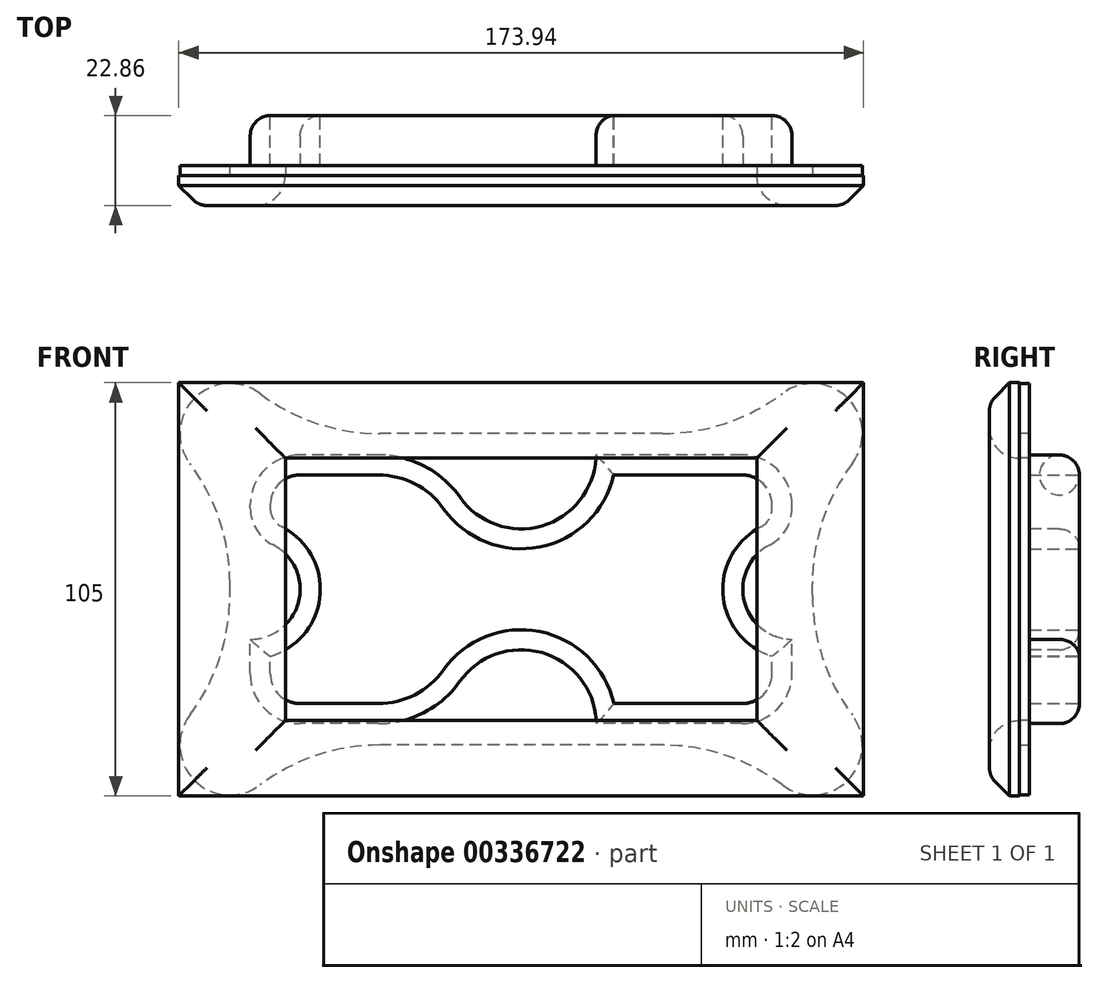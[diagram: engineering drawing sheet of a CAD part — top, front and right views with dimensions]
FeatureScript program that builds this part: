
annotation { "Feature Type Name" : "Feature", "Feature Type Description" : "" }
export const myFeature = defineFeature(function(context is Context, id is Id, definition is map)
    precondition{}
    {
        {
            var Q0;
            Q0=qCreatedBy(makeId("Front.planeOp"),FACE);
            var sketch = newSketch(context, id + "F0", { "sketchPlane" : qUnion([Q0])});
            skLineSegment(sketch, "E0.bottom", {"start": v(68.82, -34.13) * mm, "end": v(-68.82, -34.13) * mm});
            skLineSegment(sketch, "E0.top", {"start": v(68.82, 34.13) * mm, "end": v(-68.82, 34.13) * mm});
            skLineSegment(sketch, "E0.left", {"start": v(68.82, -34.13) * mm, "end": v(68.82, 34.13) * mm});
            skLineSegment(sketch, "E0.right", {"start": v(-68.82, -34.13) * mm, "end": v(-68.82, 34.13) * mm});
            skPoint(sketch, "E0.middle", {"position": v(0, 0) * mm});
            skSolve(sketch);
        }
        {
            var Q0;
            Q0 = qSketchRegion(id + "F0", true);
            extrude(context, id + "F1", {"entities" : qUnion([Q0]), "depth" : 12.7 * mm});
        }
        {
            var Q0;
            Q0=makeQuery(id+"F1.opExtrude","SWEPT_EDGE",EDGE,{"disambiguationData":[OSD([sQuery(id+"F0.wireOp",EDGE,"E0.top"),sQuery(id+"F0.wireOp",EDGE,"E0.right")])]});
            var Q1;
            Q1=makeQuery(id+"F1.opExtrude","SWEPT_EDGE",EDGE,{"disambiguationData":[OSD([sQuery(id+"F0.wireOp",EDGE,"E0.top"),sQuery(id+"F0.wireOp",EDGE,"E0.left")])]});
            var Q2;
            Q2=makeQuery(id+"F1.opExtrude","SWEPT_EDGE",EDGE,{"disambiguationData":[OSD([sQuery(id+"F0.wireOp",EDGE,"E0.bottom"),sQuery(id+"F0.wireOp",EDGE,"E0.left")])]});
            var Q3;
            Q3=makeQuery(id+"F1.opExtrude","SWEPT_EDGE",EDGE,{"disambiguationData":[OSD([sQuery(id+"F0.wireOp",EDGE,"E0.bottom"),sQuery(id+"F0.wireOp",EDGE,"E0.right")])]});
            fillet(context, id + "F2", {"entities" : qUnion([Q0, Q1, Q2, Q3]), "radius" : 12.7 * mm, "tangentPropagation" : true, "allowEdgeOverflow" : false});
        }
        {
            var Q0;
            Q0=makeQuery(id+"F1.opExtrude","CAP_FACE",FACE,{"disambiguationData":[OSD([sQuery(id+"F0.wireOp",EDGE,"E0.bottom"),sQuery(id+"F0.wireOp",EDGE,"E0.top"),sQuery(id+"F0.wireOp",EDGE,"E0.left"),sQuery(id+"F0.wireOp",EDGE,"E0.right")])],"isStart":false});
            var sketch = newSketch(context, id + "F3", { "sketchPlane" : qUnion([Q0])});
            skPoint(sketch, "E1", {"position": v(68.82, 0) * mm});
            skPoint(sketch, "E2", {"position": v(-68.82, 0) * mm});
            skPoint(sketch, "E3", {"position": v(0, 34.13) * mm});
            skPoint(sketch, "E4", {"position": v(0, -34.13) * mm});
            skCircle(sketch, "E5", {"center": v(-68.82, 0) * mm, "radius": 12.7 * mm});
            skSolve(sketch);
        }
        {
            var Q0;
            {var subQ3=sQuery(id+"F0.wireOp",EDGE,"E0.bottom");Q0=makeQuery(id+"F3.imprint","IMPRINT",FACE,{"disambiguationData":[TD([[makeQuery(id+"F3.imprint","IMPRINT",EDGE,{"derivedFrom":makeQuery(id+"F1.opExtrude","CAP_EDGE",EDGE,{"disambiguationData":[OSD([subQ3])],"isStart":false})}),-1.0]])]});}
            var sketch = newSketch(context, id + "F4", { "sketchPlane" : qUnion([Q0])});
            skCircle(sketch, "E6", {"center": v(69, 0) * mm, "radius": 12.7 * mm});
            skCircle(sketch, "E7", {"center": v(0, 34.4) * mm, "radius": 19.03 * mm});
            skCircle(sketch, "E8", {"center": v(0, -34.48) * mm, "radius": 19.12 * mm});
            skSolve(sketch);
        }
        {
            var Q0;
            {var subQ0=sQuery(id+"F4.wireOp",EDGE,"E8");var subQ1=makeQuery(id+"F3.imprint","IMPRINT",EDGE,{"derivedFrom":makeQuery(id+"F1.opExtrude","CAP_EDGE",EDGE,{"disambiguationData":[OSD([sQuery(id+"F0.wireOp",EDGE,"E0.bottom")])],"isStart":false})});var subQ2=makeQuery(id+"F4.imprint","INTERSECT",VERTEX,{"disambiguationData":[OD(0.0)],"derivedFrom":[subQ1,subQ0]});Q0=makeQuery(id+"F4.imprint","IMPRINT",FACE,{"disambiguationData":[TD([[makeQuery(id+"F4.imprint","IMPRINT",EDGE,{"disambiguationData":[TD([[subQ2,-1.0]])],"derivedFrom":subQ0}),1.0]])]});}
            var Q1;
            {var subQ0=sQuery(id+"F4.wireOp",EDGE,"E7");var subQ1=makeQuery(id+"F3.imprint","IMPRINT",EDGE,{"derivedFrom":makeQuery(id+"F1.opExtrude","CAP_EDGE",EDGE,{"disambiguationData":[OSD([sQuery(id+"F0.wireOp",EDGE,"E0.top")])],"isStart":false})});var subQ2=makeQuery(id+"F4.imprint","INTERSECT",VERTEX,{"disambiguationData":[OD(0.0)],"derivedFrom":[subQ1,subQ0]});Q1=makeQuery(id+"F4.imprint","IMPRINT",FACE,{"disambiguationData":[TD([[makeQuery(id+"F4.imprint","IMPRINT",EDGE,{"disambiguationData":[TD([[subQ2,1.0]])],"derivedFrom":subQ0}),1.0]])]});}
            extrude(context, id + "F5", {"entities" : qUnion([Q0, Q1]), "operationType" : NewBodyOperationType.REMOVE, "oppositeDirection" : true, "depth" : 25.4 * mm});
        }
        {
            var Q0;
            {var subQ0=sQuery(id+"F4.wireOp",EDGE,"E8");var subQ1=sQuery(id+"F0.wireOp",EDGE,"E0.bottom");Q0=makeQuery(id+"F5.boolean.opBoolean","COPY",EDGE,{"derivedFrom":makeQuery(id+"F5.opExtrude","SWEPT_EDGE",EDGE,{"disambiguationData":[OSD([subQ1,subQ0]),TDD([makeQuery(id+"F4.imprint","INTERSECT",VERTEX,{"disambiguationData":[OD(1.0)],"derivedFrom":[makeQuery(id+"F3.imprint","IMPRINT",EDGE,{"derivedFrom":makeQuery(id+"F1.opExtrude","CAP_EDGE",EDGE,{"disambiguationData":[OSD([subQ1])],"isStart":false})}),subQ0]})])]})});}
            var Q1;
            {var subQ0=sQuery(id+"F4.wireOp",EDGE,"E8");var subQ1=sQuery(id+"F0.wireOp",EDGE,"E0.bottom");Q1=makeQuery(id+"F5.boolean.opBoolean","COPY",EDGE,{"derivedFrom":makeQuery(id+"F5.opExtrude","SWEPT_EDGE",EDGE,{"disambiguationData":[OSD([subQ1,subQ0]),TDD([makeQuery(id+"F4.imprint","INTERSECT",VERTEX,{"disambiguationData":[OD(0.0)],"derivedFrom":[makeQuery(id+"F3.imprint","IMPRINT",EDGE,{"derivedFrom":makeQuery(id+"F1.opExtrude","CAP_EDGE",EDGE,{"disambiguationData":[OSD([subQ1])],"isStart":false})}),subQ0]})])]})});}
            var Q2;
            {var subQ0=sQuery(id+"F4.wireOp",EDGE,"E7");var subQ1=sQuery(id+"F0.wireOp",EDGE,"E0.top");Q2=makeQuery(id+"F5.boolean.opBoolean","COPY",EDGE,{"derivedFrom":makeQuery(id+"F5.opExtrude","SWEPT_EDGE",EDGE,{"disambiguationData":[OSD([subQ1,subQ0]),TDD([makeQuery(id+"F4.imprint","INTERSECT",VERTEX,{"disambiguationData":[OD(1.0)],"derivedFrom":[makeQuery(id+"F3.imprint","IMPRINT",EDGE,{"derivedFrom":makeQuery(id+"F1.opExtrude","CAP_EDGE",EDGE,{"disambiguationData":[OSD([subQ1])],"isStart":false})}),subQ0]})])]})});}
            var Q3;
            {var subQ0=sQuery(id+"F4.wireOp",EDGE,"E7");var subQ1=sQuery(id+"F0.wireOp",EDGE,"E0.top");Q3=makeQuery(id+"F5.boolean.opBoolean","COPY",EDGE,{"derivedFrom":makeQuery(id+"F5.opExtrude","SWEPT_EDGE",EDGE,{"disambiguationData":[OSD([subQ1,subQ0]),TDD([makeQuery(id+"F4.imprint","INTERSECT",VERTEX,{"disambiguationData":[OD(0.0)],"derivedFrom":[makeQuery(id+"F3.imprint","IMPRINT",EDGE,{"derivedFrom":makeQuery(id+"F1.opExtrude","CAP_EDGE",EDGE,{"disambiguationData":[OSD([subQ1])],"isStart":false})}),subQ0]})])]})});}
            fillet(context, id + "F6", {"entities" : qUnion([Q0, Q1, Q2, Q3]), "radius" : 25.4 * mm, "tangentPropagation" : true, "allowEdgeOverflow" : false});
        }
        {
            var Q0;
            {var subQ3=sQuery(id+"F0.wireOp",EDGE,"E0.bottom");Q0=makeQuery(id+"F3.imprint","IMPRINT",FACE,{"disambiguationData":[TD([[makeQuery(id+"F3.imprint","IMPRINT",EDGE,{"derivedFrom":makeQuery(id+"F1.opExtrude","CAP_EDGE",EDGE,{"disambiguationData":[OSD([subQ3])],"isStart":false})}),-1.0]])]});}
            var sketch = newSketch(context, id + "F7", { "sketchPlane" : qUnion([Q0])});
            skSolve(sketch);
        }
        {
            var Q0;
            {var subQ0=sQuery(id+"F3.wireOp",EDGE,"E5");var subQ1=makeQuery(id+"F1.opExtrude","CAP_EDGE",EDGE,{"disambiguationData":[OSD([sQuery(id+"F0.wireOp",EDGE,"E0.right")])],"isStart":false});var subQ2=makeQuery(id+"F3.imprint","INTERSECT",VERTEX,{"disambiguationData":[OD(0.0)],"derivedFrom":[subQ1,subQ0]});Q0=makeQuery(id+"F3.imprint","IMPRINT",FACE,{"disambiguationData":[TD([[makeQuery(id+"F3.imprint","IMPRINT",EDGE,{"disambiguationData":[TD([[subQ2,-1.0]])],"derivedFrom":subQ0}),1.0]])]});}
            var Q1;
            Q1=sQuery(id+"F3.wireOp",EDGE,"E5");
            extrude(context, id + "F8", {"entities" : qUnion([Q0]), "operationType" : NewBodyOperationType.REMOVE, "surfaceEntities" : qUnion([Q1]), "oppositeDirection" : true, "depth" : 25.4 * mm});
        }
        {
            var Q0;
            {var subQ3=sQuery(id+"F0.wireOp",EDGE,"E0.bottom");Q0=makeQuery(id+"F7.imprint","IMPRINT",FACE,{"disambiguationData":[TD([[makeQuery(id+"F7.imprint","IMPRINT",EDGE,{"derivedFrom":makeQuery(id+"F3.imprint","IMPRINT",EDGE,{"derivedFrom":makeQuery(id+"F1.opExtrude","CAP_EDGE",EDGE,{"disambiguationData":[OSD([subQ3])],"isStart":false})})}),-1.0]])]});}
            var sketch = newSketch(context, id + "F9", { "sketchPlane" : qUnion([Q0])});
            skPoint(sketch, "E9", {"position": v(69, 0) * mm});
            skCircle(sketch, "E10", {"center": v(69, 0) * mm, "radius": 12.7 * mm});
            skSolve(sketch);
        }
        {
            var Q0;
            {var subQ0=sQuery(id+"F9.wireOp",EDGE,"E10");var subQ1=makeQuery(id+"F7.imprint","IMPRINT",EDGE,{"derivedFrom":makeQuery(id+"F3.imprint","IMPRINT",EDGE,{"derivedFrom":makeQuery(id+"F1.opExtrude","CAP_EDGE",EDGE,{"disambiguationData":[OSD([sQuery(id+"F0.wireOp",EDGE,"E0.left")])],"isStart":false})})});var subQ2=makeQuery(id+"F9.imprint","INTERSECT",VERTEX,{"disambiguationData":[OD(0.0)],"derivedFrom":[subQ1,subQ0]});Q0=makeQuery(id+"F9.imprint","IMPRINT",FACE,{"disambiguationData":[TD([[makeQuery(id+"F9.imprint","IMPRINT",EDGE,{"disambiguationData":[TD([[subQ2,1.0]])],"derivedFrom":subQ0}),1.0]])]});}
            extrude(context, id + "F10", {"entities" : qUnion([Q0]), "operationType" : NewBodyOperationType.REMOVE, "oppositeDirection" : true, "depth" : 25.4 * mm});
        }
        {
            var Q0;
            {var subQ0=sQuery(id+"F3.wireOp",EDGE,"E5");var subQ1=sQuery(id+"F0.wireOp",EDGE,"E0.right");Q0=makeQuery(id+"F8.boolean.opBoolean","COPY",EDGE,{"derivedFrom":makeQuery(id+"F8.opExtrude","SWEPT_EDGE",EDGE,{"disambiguationData":[OSD([subQ1,subQ0]),TDD([makeQuery(id+"F3.imprint","INTERSECT",VERTEX,{"disambiguationData":[OD(1.0)],"derivedFrom":[makeQuery(id+"F1.opExtrude","CAP_EDGE",EDGE,{"disambiguationData":[OSD([subQ1])],"isStart":false}),subQ0]})])]})});}
            var Q1;
            {var subQ0=sQuery(id+"F3.wireOp",EDGE,"E5");var subQ1=sQuery(id+"F0.wireOp",EDGE,"E0.right");Q1=makeQuery(id+"F8.boolean.opBoolean","COPY",EDGE,{"derivedFrom":makeQuery(id+"F8.opExtrude","SWEPT_EDGE",EDGE,{"disambiguationData":[OSD([subQ1,subQ0]),TDD([makeQuery(id+"F3.imprint","INTERSECT",VERTEX,{"disambiguationData":[OD(0.0)],"derivedFrom":[makeQuery(id+"F1.opExtrude","CAP_EDGE",EDGE,{"disambiguationData":[OSD([subQ1])],"isStart":false}),subQ0]})])]})});}
            var Q2;
            {var subQ0=sQuery(id+"F9.wireOp",EDGE,"E10");var subQ1=sQuery(id+"F0.wireOp",EDGE,"E0.left");Q2=makeQuery(id+"F10.boolean.opBoolean","COPY",EDGE,{"derivedFrom":makeQuery(id+"F10.opExtrude","SWEPT_EDGE",EDGE,{"disambiguationData":[OSD([subQ1,subQ0]),TDD([makeQuery(id+"F9.imprint","INTERSECT",VERTEX,{"disambiguationData":[OD(0.0)],"derivedFrom":[makeQuery(id+"F7.imprint","IMPRINT",EDGE,{"derivedFrom":makeQuery(id+"F3.imprint","IMPRINT",EDGE,{"derivedFrom":makeQuery(id+"F1.opExtrude","CAP_EDGE",EDGE,{"disambiguationData":[OSD([subQ1])],"isStart":false})})}),subQ0]})])]})});}
            var Q3;
            {var subQ0=sQuery(id+"F9.wireOp",EDGE,"E10");var subQ1=sQuery(id+"F0.wireOp",EDGE,"E0.left");Q3=makeQuery(id+"F10.boolean.opBoolean","COPY",EDGE,{"derivedFrom":makeQuery(id+"F10.opExtrude","SWEPT_EDGE",EDGE,{"disambiguationData":[OSD([subQ1,subQ0]),TDD([makeQuery(id+"F9.imprint","INTERSECT",VERTEX,{"disambiguationData":[OD(1.0)],"derivedFrom":[makeQuery(id+"F7.imprint","IMPRINT",EDGE,{"derivedFrom":makeQuery(id+"F3.imprint","IMPRINT",EDGE,{"derivedFrom":makeQuery(id+"F1.opExtrude","CAP_EDGE",EDGE,{"disambiguationData":[OSD([subQ1])],"isStart":false})})}),subQ0]})])]})});}
            fillet(context, id + "F11", {"entities" : qUnion([Q0, Q1, Q2, Q3]), "radius" : 10.4 * mm, "tangentPropagation" : true, "allowEdgeOverflow" : false});
        }
        {
            var Q0;
            Q0=makeQuery(id+"F1.opExtrude","CAP_FACE",FACE,{"disambiguationData":[OSD([sQuery(id+"F0.wireOp",EDGE,"E0.bottom"),sQuery(id+"F0.wireOp",EDGE,"E0.top"),sQuery(id+"F0.wireOp",EDGE,"E0.left"),sQuery(id+"F0.wireOp",EDGE,"E0.right")])],"isStart":true});
            fillet(context, id + "F12", {"entities" : qUnion([Q0]), "radius" : 5.08 * mm, "tangentPropagation" : true, "allowEdgeOverflow" : false});
        }
        {
            var Q0;
            Q0=makeQuery(id+"F1.opExtrude","CAP_FACE",FACE,{"disambiguationData":[OSD([sQuery(id+"F0.wireOp",EDGE,"E0.bottom"),sQuery(id+"F0.wireOp",EDGE,"E0.top"),sQuery(id+"F0.wireOp",EDGE,"E0.left"),sQuery(id+"F0.wireOp",EDGE,"E0.right")])],"isStart":true});
            var sketch = newSketch(context, id + "F13", { "sketchPlane" : qUnion([Q0])});
            skSolve(sketch);
        }
        {
            var Q0;
            Q0 = qSketchRegion(id + "F13", true);
            var Q1;
            {var subQ0=sQuery(id+"F0.wireOp",EDGE,"E0.right");var subQ1=sQuery(id+"F0.wireOp",EDGE,"E0.left");var subQ2=sQuery(id+"F0.wireOp",EDGE,"E0.top");var subQ3=sQuery(id+"F0.wireOp",EDGE,"E0.bottom");var subQ4=makeQuery(id+"F1.opExtrude","CAP_FACE",FACE,{"disambiguationData":[OSD([subQ3,subQ2,subQ1,subQ0])],"isStart":true});var subQ5=subQ4;var subQ6=subQ5;var subQ7=subQ6;var subQ8=subQ7;var subQ9=subQ8;var subQ10=subQ9;var subQ23=sQuery(id+"F4.wireOp",EDGE,"E7");var subQ24=makeQuery(id+"F5.opExtrude","SWEPT_FACE",FACE,{"disambiguationData":[OSD([subQ23])]});Q1=makeQuery(id+"F13.imprint","IMPRINT",FACE,{"disambiguationData":[TD([[makeQuery(id+"F13.imprint","IMPRINT",EDGE,{"derivedFrom":makeQuery(id+"F12.opFillet","BLEND_EDGE",EDGE,{"blendedFrom":[makeQuery(id+"F5.boolean.opBoolean","INTERSECT",EDGE,{"derivedFrom":[subQ5,subQ24]}),subQ10],"blendedInto":[subQ10]})}),1.0]])]});}
            extrude(context, id + "F14", {"entities" : qUnion([Q0, Q1]), "operationType" : NewBodyOperationType.REMOVE, "oppositeDirection" : true, "depth" : 25.4 * mm});
        }
        {
            var Q0;
            {var subQ3=sQuery(id+"F0.wireOp",EDGE,"E0.bottom");Q0=makeQuery(id+"F7.imprint","IMPRINT",FACE,{"disambiguationData":[TD([[makeQuery(id+"F7.imprint","IMPRINT",EDGE,{"derivedFrom":makeQuery(id+"F3.imprint","IMPRINT",EDGE,{"derivedFrom":makeQuery(id+"F1.opExtrude","CAP_EDGE",EDGE,{"disambiguationData":[OSD([subQ3])],"isStart":false})})}),-1.0]])]});}
            var sketch = newSketch(context, id + "F15", { "sketchPlane" : qUnion([Q0])});
            skLineSegment(sketch, "E11.bottom", {"start": v(74, -39.58) * mm, "end": v(-74, -39.58) * mm});
            skLineSegment(sketch, "E11.top", {"start": v(74, 39.58) * mm, "end": v(-74, 39.58) * mm});
            skLineSegment(sketch, "E11.left", {"start": v(74, -39.58) * mm, "end": v(74, 39.58) * mm});
            skLineSegment(sketch, "E11.right", {"start": v(-74, -39.58) * mm, "end": v(-74, 39.58) * mm});
            skPoint(sketch, "E11.middle", {"position": v(0, 0) * mm});
            skSolve(sketch);
        }
        {
            var Q0;
            Q0 = qSketchRegion(id + "F15", true);
            extrude(context, id + "F16", {"entities" : qUnion([Q0]), "operationType" : NewBodyOperationType.ADD, "depth" : 2.54 * mm});
        }
        {
            var Q0;
            Q0=makeQuery(id+"F16.opExtrude","CAP_FACE",FACE,{"disambiguationData":[OSD([sQuery(id+"F15.wireOp",EDGE,"E11.bottom"),sQuery(id+"F15.wireOp",EDGE,"E11.top"),sQuery(id+"F15.wireOp",EDGE,"E11.left"),sQuery(id+"F15.wireOp",EDGE,"E11.right")])],"isStart":false});
            var sketch = newSketch(context, id + "F17", { "sketchPlane" : qUnion([Q0])});
            skPoint(sketch, "E12", {"position": v(-74, 39.58) * mm});
            skPoint(sketch, "E13", {"position": v(74, 39.58) * mm});
            skPoint(sketch, "E14", {"position": v(74, -39.58) * mm});
            skPoint(sketch, "E15", {"position": v(-74, -39.58) * mm});
            skCircle(sketch, "E16", {"center": v(-74, 39.58) * mm, "radius": 12.7 * mm});
            skCircle(sketch, "E17", {"center": v(74, 39.58) * mm, "radius": 12.7 * mm});
            skCircle(sketch, "E18", {"center": v(-74, -39.58) * mm, "radius": 12.7 * mm});
            skCircle(sketch, "E19", {"center": v(74, -39.58) * mm, "radius": 12.7 * mm});
            skSolve(sketch);
        }
        {
            var Q0;
            Q0 = qSketchRegion(id + "F17", true);
            extrude(context, id + "F18", {"entities" : qUnion([Q0]), "operationType" : NewBodyOperationType.ADD, "oppositeDirection" : true, "depth" : 2.54 * mm});
        }
        {
            var Q0;
            Q0=makeQuery(id+"F18.boolean.opBoolean","INTERSECT",EDGE,{"derivedFrom":[makeQuery(id+"F16.opExtrude","SWEPT_FACE",FACE,{"disambiguationData":[OSD([sQuery(id+"F15.wireOp",EDGE,"E11.top")])]}),makeQuery(id+"F18.opExtrude","SWEPT_FACE",FACE,{"disambiguationData":[OSD([sQuery(id+"F17.wireOp",EDGE,"E17")])]})]});
            var Q1;
            Q1=makeQuery(id+"F18.boolean.opBoolean","INTERSECT",EDGE,{"derivedFrom":[makeQuery(id+"F16.opExtrude","SWEPT_FACE",FACE,{"disambiguationData":[OSD([sQuery(id+"F15.wireOp",EDGE,"E11.top")])]}),makeQuery(id+"F18.opExtrude","SWEPT_FACE",FACE,{"disambiguationData":[OSD([sQuery(id+"F17.wireOp",EDGE,"E16")])]})]});
            fillet(context, id + "F19", {"entities" : qUnion([Q0, Q1]), "radius" : 50.8 * mm, "tangentPropagation" : true, "allowEdgeOverflow" : false});
        }
        {
            var Q0;
            Q0=makeQuery(id+"F18.boolean.opBoolean","INTERSECT",EDGE,{"derivedFrom":[makeQuery(id+"F16.opExtrude","SWEPT_FACE",FACE,{"disambiguationData":[OSD([sQuery(id+"F15.wireOp",EDGE,"E11.right")])]}),makeQuery(id+"F18.opExtrude","SWEPT_FACE",FACE,{"disambiguationData":[OSD([sQuery(id+"F17.wireOp",EDGE,"E16")])]})]});
            var Q1;
            Q1=makeQuery(id+"F18.boolean.opBoolean","INTERSECT",EDGE,{"derivedFrom":[makeQuery(id+"F16.opExtrude","SWEPT_FACE",FACE,{"disambiguationData":[OSD([sQuery(id+"F15.wireOp",EDGE,"E11.bottom")])]}),makeQuery(id+"F18.opExtrude","SWEPT_FACE",FACE,{"disambiguationData":[OSD([sQuery(id+"F17.wireOp",EDGE,"E18")])]})]});
            var Q2;
            Q2=makeQuery(id+"F18.boolean.opBoolean","INTERSECT",EDGE,{"derivedFrom":[makeQuery(id+"F16.opExtrude","SWEPT_FACE",FACE,{"disambiguationData":[OSD([sQuery(id+"F15.wireOp",EDGE,"E11.bottom")])]}),makeQuery(id+"F18.opExtrude","SWEPT_FACE",FACE,{"disambiguationData":[OSD([sQuery(id+"F17.wireOp",EDGE,"E19")])]})]});
            fillet(context, id + "F20", {"entities" : qUnion([Q0, Q1, Q2]), "radius" : 50.8 * mm, "tangentPropagation" : true, "allowEdgeOverflow" : false});
        }
        {
            var Q0;
            Q0=makeQuery(id+"F18.boolean.opBoolean","INTERSECT",EDGE,{"derivedFrom":[makeQuery(id+"F16.opExtrude","SWEPT_FACE",FACE,{"disambiguationData":[OSD([sQuery(id+"F15.wireOp",EDGE,"E11.right")])]}),makeQuery(id+"F18.opExtrude","SWEPT_FACE",FACE,{"disambiguationData":[OSD([sQuery(id+"F17.wireOp",EDGE,"E18")])]})]});
            fillet(context, id + "F21", {"entities" : qUnion([Q0]), "radius" : 50.8 * mm, "tangentPropagation" : true, "allowEdgeOverflow" : false});
        }
        {
            var Q0;
            Q0=makeQuery(id+"F18.boolean.opBoolean","INTERSECT",EDGE,{"derivedFrom":[makeQuery(id+"F16.opExtrude","SWEPT_FACE",FACE,{"disambiguationData":[OSD([sQuery(id+"F15.wireOp",EDGE,"E11.left")])]}),makeQuery(id+"F18.opExtrude","SWEPT_FACE",FACE,{"disambiguationData":[OSD([sQuery(id+"F17.wireOp",EDGE,"E19")])]})]});
            var Q1;
            Q1=makeQuery(id+"F18.boolean.opBoolean","INTERSECT",EDGE,{"derivedFrom":[makeQuery(id+"F16.opExtrude","SWEPT_FACE",FACE,{"disambiguationData":[OSD([sQuery(id+"F15.wireOp",EDGE,"E11.left")])]}),makeQuery(id+"F18.opExtrude","SWEPT_FACE",FACE,{"disambiguationData":[OSD([sQuery(id+"F17.wireOp",EDGE,"E17")])]})]});
            fillet(context, id + "F22", {"entities" : qUnion([Q0, Q1]), "radius" : 50.8 * mm, "tangentPropagation" : true, "allowEdgeOverflow" : false});
        }
        {
            var Q0;
            Q0=makeQuery(id+"F18.boolean.opBoolean","MERGE",FACE,{"derivedFrom":[makeQuery(id+"F16.opExtrude","CAP_FACE",FACE,{"disambiguationData":[OSD([sQuery(id+"F15.wireOp",EDGE,"E11.bottom"),sQuery(id+"F15.wireOp",EDGE,"E11.top"),sQuery(id+"F15.wireOp",EDGE,"E11.left"),sQuery(id+"F15.wireOp",EDGE,"E11.right")])],"isStart":false}),makeQuery(id+"F18.opExtrude","CAP_FACE",FACE,{"disambiguationData":[OSD([sQuery(id+"F17.wireOp",EDGE,"E16")])],"isStart":true}),makeQuery(id+"F18.opExtrude","CAP_FACE",FACE,{"disambiguationData":[OSD([sQuery(id+"F17.wireOp",EDGE,"E17")])],"isStart":true}),makeQuery(id+"F18.opExtrude","CAP_FACE",FACE,{"disambiguationData":[OSD([sQuery(id+"F17.wireOp",EDGE,"E18")])],"isStart":true}),makeQuery(id+"F18.opExtrude","CAP_FACE",FACE,{"disambiguationData":[OSD([sQuery(id+"F17.wireOp",EDGE,"E19")])],"isStart":true})]});
            var sketch = newSketch(context, id + "F23", { "sketchPlane" : qUnion([Q0])});
            skLineSegment(sketch, "E20.bottom", {"start": v(-86.97, 52.5) * mm, "end": v(86.97, 52.5) * mm});
            skLineSegment(sketch, "E20.top", {"start": v(-86.97, -52.5) * mm, "end": v(86.97, -52.5) * mm});
            skLineSegment(sketch, "E20.left", {"start": v(-86.97, 52.5) * mm, "end": v(-86.97, -52.5) * mm});
            skLineSegment(sketch, "E20.right", {"start": v(86.97, 52.5) * mm, "end": v(86.97, -52.5) * mm});
            skPoint(sketch, "E20.middle", {"position": v(0, 0) * mm});
            skSolve(sketch);
        }
        {
            var Q0;
            {var subQ6=sQuery(id+"F15.wireOp",EDGE,"E11.top");Q0=makeQuery(id+"F23.imprint","IMPRINT",FACE,{"disambiguationData":[TD([[makeQuery(id+"F23.imprint","IMPRINT",EDGE,{"derivedFrom":makeQuery(id+"F16.opExtrude","CAP_EDGE",EDGE,{"disambiguationData":[OSD([subQ6])],"isStart":false})}),1.0]])]});}
            var Q1;
            Q1=makeQuery(id+"F23.imprint","IMPRINT",FACE,{"disambiguationData":[TD([[makeQuery(id+"F23.imprint","IMPRINT",EDGE,{"derivedFrom":sQuery(id+"F23.wireOp",EDGE,"E20.bottom")}),-1.0]])]});
            extrude(context, id + "F24", {"entities" : qUnion([Q0, Q1]), "operationType" : NewBodyOperationType.ADD, "depth" : 7.62 * mm});
        }
        {
            var Q0;
            Q0=makeQuery(id+"F24.opExtrude","CAP_EDGE",EDGE,{"disambiguationData":[OSD([sQuery(id+"F23.wireOp",EDGE,"E20.bottom")])],"isStart":false});
            var Q1;
            Q1=makeQuery(id+"F24.opExtrude","CAP_EDGE",EDGE,{"disambiguationData":[OSD([sQuery(id+"F23.wireOp",EDGE,"E20.left")])],"isStart":false});
            var Q2;
            Q2=makeQuery(id+"F24.opExtrude","CAP_EDGE",EDGE,{"disambiguationData":[OSD([sQuery(id+"F23.wireOp",EDGE,"E20.top")])],"isStart":false});
            var Q3;
            Q3=makeQuery(id+"F24.opExtrude","CAP_EDGE",EDGE,{"disambiguationData":[OSD([sQuery(id+"F23.wireOp",EDGE,"E20.right")])],"isStart":false});
            chamfer(context, id + "F25", {"entities" : qUnion([Q0, Q1, Q2, Q3]), "width" : 5.08 * mm, "tangentPropagation" : true});
        }
        {
            var Q0;
            {var subQ0=sQuery(id+"F23.wireOp",EDGE,"E20.left");Q0=makeQuery(id+"F25.opChamfer","BLEND_EDGE",EDGE,{"blendedFrom":[makeQuery(id+"F24.opExtrude","CAP_EDGE",EDGE,{"disambiguationData":[OSD([subQ0])],"isStart":false}),makeQuery(id+"F24.opExtrude","CAP_FACE",FACE,{"disambiguationData":[OSD([sQuery(id+"F23.wireOp",EDGE,"E20.bottom"),sQuery(id+"F23.wireOp",EDGE,"E20.top"),subQ0,sQuery(id+"F23.wireOp",EDGE,"E20.right")])],"isStart":false})],"blendedInto":[makeQuery(id+"F24.opExtrude","CAP_FACE",FACE,{"disambiguationData":[OSD([sQuery(id+"F23.wireOp",EDGE,"E20.bottom"),sQuery(id+"F23.wireOp",EDGE,"E20.top"),subQ0,sQuery(id+"F23.wireOp",EDGE,"E20.right")])],"isStart":false})]});}
            var Q1;
            {var subQ0=sQuery(id+"F23.wireOp",EDGE,"E20.top");Q1=makeQuery(id+"F25.opChamfer","BLEND_EDGE",EDGE,{"blendedFrom":[makeQuery(id+"F24.opExtrude","CAP_EDGE",EDGE,{"disambiguationData":[OSD([subQ0])],"isStart":false}),makeQuery(id+"F24.opExtrude","CAP_FACE",FACE,{"disambiguationData":[OSD([sQuery(id+"F23.wireOp",EDGE,"E20.bottom"),subQ0,sQuery(id+"F23.wireOp",EDGE,"E20.left"),sQuery(id+"F23.wireOp",EDGE,"E20.right")])],"isStart":false})],"blendedInto":[makeQuery(id+"F24.opExtrude","CAP_FACE",FACE,{"disambiguationData":[OSD([sQuery(id+"F23.wireOp",EDGE,"E20.bottom"),subQ0,sQuery(id+"F23.wireOp",EDGE,"E20.left"),sQuery(id+"F23.wireOp",EDGE,"E20.right")])],"isStart":false})]});}
            var Q2;
            {var subQ0=sQuery(id+"F23.wireOp",EDGE,"E20.bottom");Q2=makeQuery(id+"F25.opChamfer","BLEND_EDGE",EDGE,{"blendedFrom":[makeQuery(id+"F24.opExtrude","CAP_EDGE",EDGE,{"disambiguationData":[OSD([subQ0])],"isStart":false}),makeQuery(id+"F24.opExtrude","CAP_FACE",FACE,{"disambiguationData":[OSD([subQ0,sQuery(id+"F23.wireOp",EDGE,"E20.top"),sQuery(id+"F23.wireOp",EDGE,"E20.left"),sQuery(id+"F23.wireOp",EDGE,"E20.right")])],"isStart":false})],"blendedInto":[makeQuery(id+"F24.opExtrude","CAP_FACE",FACE,{"disambiguationData":[OSD([subQ0,sQuery(id+"F23.wireOp",EDGE,"E20.top"),sQuery(id+"F23.wireOp",EDGE,"E20.left"),sQuery(id+"F23.wireOp",EDGE,"E20.right")])],"isStart":false})]});}
            var Q3;
            {var subQ0=sQuery(id+"F23.wireOp",EDGE,"E20.right");Q3=makeQuery(id+"F25.opChamfer","BLEND_EDGE",EDGE,{"blendedFrom":[makeQuery(id+"F24.opExtrude","CAP_EDGE",EDGE,{"disambiguationData":[OSD([subQ0])],"isStart":false}),makeQuery(id+"F24.opExtrude","CAP_FACE",FACE,{"disambiguationData":[OSD([sQuery(id+"F23.wireOp",EDGE,"E20.bottom"),sQuery(id+"F23.wireOp",EDGE,"E20.top"),sQuery(id+"F23.wireOp",EDGE,"E20.left"),subQ0])],"isStart":false})],"blendedInto":[makeQuery(id+"F24.opExtrude","CAP_FACE",FACE,{"disambiguationData":[OSD([sQuery(id+"F23.wireOp",EDGE,"E20.bottom"),sQuery(id+"F23.wireOp",EDGE,"E20.top"),sQuery(id+"F23.wireOp",EDGE,"E20.left"),subQ0])],"isStart":false})]});}
            fillet(context, id + "F26", {"entities" : qUnion([Q0, Q1, Q2, Q3]), "radius" : 5.08 * mm, "tangentPropagation" : true, "allowEdgeOverflow" : false});
        }
        {
            var Q0;
            Q0=makeQuery(id+"F24.opExtrude","CAP_FACE",FACE,{"disambiguationData":[OSD([sQuery(id+"F23.wireOp",EDGE,"E20.bottom"),sQuery(id+"F23.wireOp",EDGE,"E20.top"),sQuery(id+"F23.wireOp",EDGE,"E20.left"),sQuery(id+"F23.wireOp",EDGE,"E20.right")])],"isStart":false});
            var sketch = newSketch(context, id + "F27", { "sketchPlane" : qUnion([Q0])});
            skLineSegment(sketch, "E21.bottom", {"start": v(-59.9, 33.33) * mm, "end": v(59.9, 33.33) * mm});
            skLineSegment(sketch, "E21.top", {"start": v(-59.9, -33.33) * mm, "end": v(59.9, -33.33) * mm});
            skLineSegment(sketch, "E21.left", {"start": v(-59.9, 33.33) * mm, "end": v(-59.9, -33.33) * mm});
            skLineSegment(sketch, "E21.right", {"start": v(59.9, 33.33) * mm, "end": v(59.9, -33.33) * mm});
            skPoint(sketch, "E21.middle", {"position": v(0, 0) * mm});
            skSolve(sketch);
        }
        {
            var Q0;
            Q0=makeQuery(id+"F27.imprint","IMPRINT",FACE,{"disambiguationData":[TD([[makeQuery(id+"F27.imprint","IMPRINT",EDGE,{"derivedFrom":sQuery(id+"F27.wireOp",EDGE,"E21.bottom")}),-1.0]])]});
            extrude(context, id + "F28", {"entities" : qUnion([Q0]), "operationType" : NewBodyOperationType.REMOVE, "oppositeDirection" : true, "depth" : 10.16 * mm});
        }
        {
            var Q0;
            Q0=makeQuery(id+"F24.opExtrude","CAP_FACE",FACE,{"disambiguationData":[OSD([sQuery(id+"F23.wireOp",EDGE,"E20.bottom"),sQuery(id+"F23.wireOp",EDGE,"E20.top"),sQuery(id+"F23.wireOp",EDGE,"E20.left"),sQuery(id+"F23.wireOp",EDGE,"E20.right")])],"isStart":false});
            fillet(context, id + "F29", {"entities" : qUnion([Q0]), "radius" : 7.62 * mm, "tangentPropagation" : true, "allowEdgeOverflow" : false});
        }
    });
